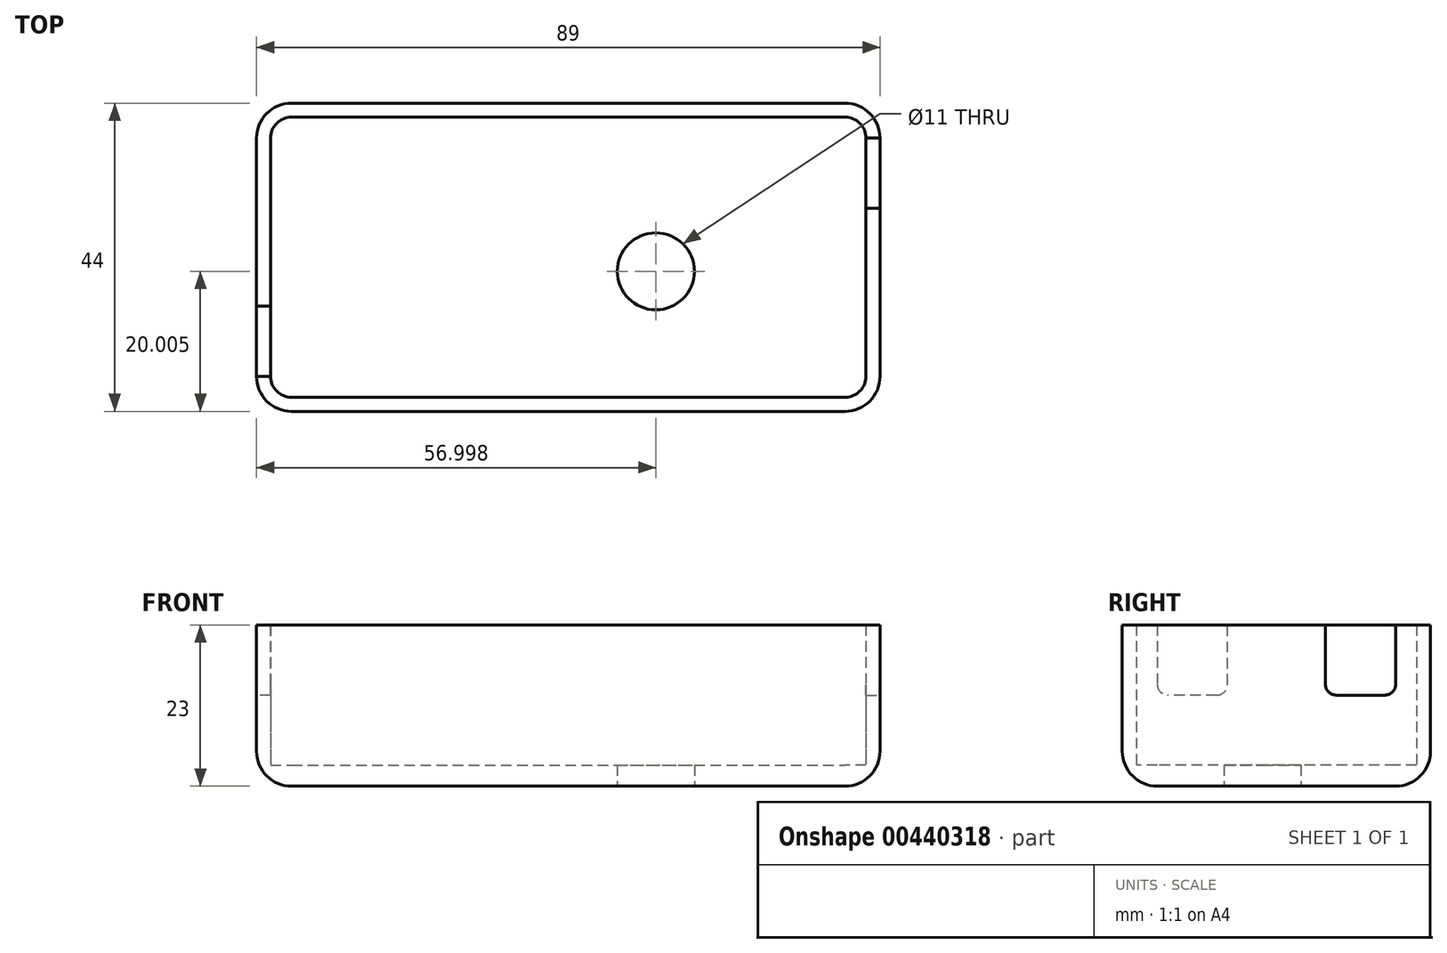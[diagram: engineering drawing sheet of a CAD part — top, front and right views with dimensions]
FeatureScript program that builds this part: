
annotation { "Feature Type Name" : "Feature", "Feature Type Description" : "" }
export const myFeature = defineFeature(function(context is Context, id is Id, definition is map)
    precondition{}
    {
        {
            var Q0;
            Q0=qCreatedBy(makeId("Top.planeOp"),FACE);
            var sketch = newSketch(context, id + "F0", { "sketchPlane" : qUnion([Q0])});
            skLineSegment(sketch, "E0.bottom", {"start": v(-41.95, 9.21) * mm, "end": v(43.05, 9.21) * mm});
            skLineSegment(sketch, "E0.top", {"start": v(-41.95, -30.79) * mm, "end": v(43.05, -30.79) * mm});
            skLineSegment(sketch, "E0.left", {"start": v(-41.95, 9.21) * mm, "end": v(-41.95, -30.79) * mm});
            skLineSegment(sketch, "E0.right", {"start": v(43.05, 9.21) * mm, "end": v(43.05, -30.79) * mm});
            skLineSegment(sketch, "E1.0", {"start": v(-43.95, -32.79) * mm, "end": v(45.05, -32.79) * mm});
            skLineSegment(sketch, "E1.1", {"start": v(-43.95, 11.21) * mm, "end": v(-43.95, -32.79) * mm});
            skLineSegment(sketch, "E1.2", {"start": v(-43.95, 11.21) * mm, "end": v(45.05, 11.21) * mm});
            skLineSegment(sketch, "E1.3", {"start": v(45.05, 11.21) * mm, "end": v(45.05, -32.79) * mm});
            skSolve(sketch);
        }
        {
            var Q0;
            Q0=makeQuery(id+"F0.imprint","IMPRINT",FACE,{"disambiguationData":[TD([[makeQuery(id+"F0.imprint","IMPRINT",EDGE,{"derivedFrom":sQuery(id+"F0.wireOp",EDGE,"E0.bottom")}),1.0]])]});
            extrude(context, id + "F1", {"entities" : qUnion([Q0]), "depth" : 20 * mm});
        }
        {
            var Q0;
            Q0=makeQuery(id+"F1.opExtrude","CAP_FACE",FACE,{"disambiguationData":[OSD([sQuery(id+"F0.wireOp",EDGE,"E0.bottom"),sQuery(id+"F0.wireOp",EDGE,"E0.top"),sQuery(id+"F0.wireOp",EDGE,"E0.left"),sQuery(id+"F0.wireOp",EDGE,"E0.right"),sQuery(id+"F0.wireOp",EDGE,"E1.0"),sQuery(id+"F0.wireOp",EDGE,"E1.1"),sQuery(id+"F0.wireOp",EDGE,"E1.2"),sQuery(id+"F0.wireOp",EDGE,"E1.3")])],"isStart":true});
            var sketch = newSketch(context, id + "F2", { "sketchPlane" : qUnion([Q0])});
            skLineSegment(sketch, "E2.bottom", {"start": v(-43.95, 32.79) * mm, "end": v(45.05, 32.79) * mm});
            skLineSegment(sketch, "E2.top", {"start": v(-43.95, -11.21) * mm, "end": v(45.05, -11.21) * mm});
            skLineSegment(sketch, "E2.left", {"start": v(-43.95, 32.79) * mm, "end": v(-43.95, -11.21) * mm});
            skLineSegment(sketch, "E2.right", {"start": v(45.05, 32.79) * mm, "end": v(45.05, -11.21) * mm});
            skSolve(sketch);
        }
        {
            var Q0;
            Q0=makeQuery(id+"F2.imprint","IMPRINT",FACE,{"disambiguationData":[TD([[makeQuery(id+"F2.imprint","IMPRINT",EDGE,{"derivedFrom":sQuery(id+"F2.wireOp",EDGE,"E2.bottom")}),-1.0]])]});
            var Q1;
            Q1=makeQuery(id+"F2.imprint","IMPRINT",FACE,{"disambiguationData":[TD([[makeQuery(id+"F2.imprint","IMPRINT",EDGE,{"derivedFrom":makeQuery(id+"F1.opExtrude","CAP_EDGE",EDGE,{"disambiguationData":[OSD([sQuery(id+"F0.wireOp",EDGE,"E0.bottom")])],"isStart":true})}),1.0]])]});
            extrude(context, id + "F3", {"entities" : qUnion([Q0, Q1]), "operationType" : NewBodyOperationType.ADD, "depth" : 3 * mm});
        }
        {
            var Q0;
            Q0=makeQuery(id+"F3.boolean.opBoolean","MERGE",EDGE,{"derivedFrom":[makeQuery(id+"F1.opExtrude","SWEPT_EDGE",EDGE,{"disambiguationData":[OSD([sQuery(id+"F0.wireOp",EDGE,"E1.0"),sQuery(id+"F0.wireOp",EDGE,"E1.1")])]}),makeQuery(id+"F3.opExtrude","SWEPT_EDGE",EDGE,{"disambiguationData":[OSD([sQuery(id+"F2.wireOp",EDGE,"E2.bottom"),sQuery(id+"F2.wireOp",EDGE,"E2.left")])]})]});
            var Q1;
            Q1=makeQuery(id+"F3.boolean.opBoolean","MERGE",EDGE,{"derivedFrom":[makeQuery(id+"F1.opExtrude","SWEPT_EDGE",EDGE,{"disambiguationData":[OSD([sQuery(id+"F0.wireOp",EDGE,"E1.0"),sQuery(id+"F0.wireOp",EDGE,"E1.3")])]}),makeQuery(id+"F3.opExtrude","SWEPT_EDGE",EDGE,{"disambiguationData":[OSD([sQuery(id+"F2.wireOp",EDGE,"E2.bottom"),sQuery(id+"F2.wireOp",EDGE,"E2.right")])]})]});
            var Q2;
            Q2=makeQuery(id+"F3.boolean.opBoolean","MERGE",EDGE,{"derivedFrom":[makeQuery(id+"F1.opExtrude","SWEPT_EDGE",EDGE,{"disambiguationData":[OSD([sQuery(id+"F0.wireOp",EDGE,"E1.2"),sQuery(id+"F0.wireOp",EDGE,"E1.3")])]}),makeQuery(id+"F3.opExtrude","SWEPT_EDGE",EDGE,{"disambiguationData":[OSD([sQuery(id+"F2.wireOp",EDGE,"E2.top"),sQuery(id+"F2.wireOp",EDGE,"E2.right")])]})]});
            var Q3;
            Q3=makeQuery(id+"F3.boolean.opBoolean","MERGE",EDGE,{"derivedFrom":[makeQuery(id+"F1.opExtrude","SWEPT_EDGE",EDGE,{"disambiguationData":[OSD([sQuery(id+"F0.wireOp",EDGE,"E1.1"),sQuery(id+"F0.wireOp",EDGE,"E1.2")])]}),makeQuery(id+"F3.opExtrude","SWEPT_EDGE",EDGE,{"disambiguationData":[OSD([sQuery(id+"F2.wireOp",EDGE,"E2.top"),sQuery(id+"F2.wireOp",EDGE,"E2.left")])]})]});
            var Q4;
            Q4=makeQuery(id+"F3.opExtrude","CAP_EDGE",EDGE,{"disambiguationData":[OSD([sQuery(id+"F2.wireOp",EDGE,"E2.left")])],"isStart":false});
            var Q5;
            Q5=makeQuery(id+"F3.opExtrude","CAP_EDGE",EDGE,{"disambiguationData":[OSD([sQuery(id+"F2.wireOp",EDGE,"E2.top")])],"isStart":false});
            var Q6;
            Q6=makeQuery(id+"F3.opExtrude","CAP_EDGE",EDGE,{"disambiguationData":[OSD([sQuery(id+"F2.wireOp",EDGE,"E2.right")])],"isStart":false});
            var Q7;
            Q7=makeQuery(id+"F3.opExtrude","CAP_EDGE",EDGE,{"disambiguationData":[OSD([sQuery(id+"F2.wireOp",EDGE,"E2.bottom")])],"isStart":false});
            fillet(context, id + "F4", {"entities" : qUnion([Q0, Q1, Q2, Q3, Q4, Q5, Q6, Q7]), "radius" : 5 * mm, "tangentPropagation" : true, "allowEdgeOverflow" : false});
        }
        {
            var Q0;
            Q0=makeQuery(id+"F1.opExtrude","SWEPT_EDGE",EDGE,{"disambiguationData":[OSD([sQuery(id+"F0.wireOp",EDGE,"E0.bottom"),sQuery(id+"F0.wireOp",EDGE,"E0.left")])]});
            var Q1;
            Q1=makeQuery(id+"F1.opExtrude","SWEPT_EDGE",EDGE,{"disambiguationData":[OSD([sQuery(id+"F0.wireOp",EDGE,"E0.top"),sQuery(id+"F0.wireOp",EDGE,"E0.left")])]});
            var Q2;
            Q2=makeQuery(id+"F1.opExtrude","SWEPT_EDGE",EDGE,{"disambiguationData":[OSD([sQuery(id+"F0.wireOp",EDGE,"E0.bottom"),sQuery(id+"F0.wireOp",EDGE,"E0.right")])]});
            var Q3;
            Q3=makeQuery(id+"F1.opExtrude","SWEPT_EDGE",EDGE,{"disambiguationData":[OSD([sQuery(id+"F0.wireOp",EDGE,"E0.top"),sQuery(id+"F0.wireOp",EDGE,"E0.right")])]});
            fillet(context, id + "F5", {"entities" : qUnion([Q0, Q1, Q2, Q3]), "radius" : 3 * mm, "tangentPropagation" : true, "allowEdgeOverflow" : false});
        }
        {
            var Q0;
            Q0=makeQuery(id+"F3.boolean.opBoolean","MERGE",FACE,{"derivedFrom":[makeQuery(id+"F1.opExtrude","SWEPT_FACE",FACE,{"disambiguationData":[OSD([sQuery(id+"F0.wireOp",EDGE,"E1.3")])]}),makeQuery(id+"F3.opExtrude","SWEPT_FACE",FACE,{"disambiguationData":[OSD([sQuery(id+"F2.wireOp",EDGE,"E2.right")])]})]});
            var sketch = newSketch(context, id + "F6", { "sketchPlane" : qUnion([Q0])});
            skLineSegment(sketch, "E3.bottom", {"start": v(6.21, 20) * mm, "end": v(-3.79, 20) * mm});
            skLineSegment(sketch, "E3.top", {"start": v(6.21, 10) * mm, "end": v(-3.79, 10) * mm});
            skLineSegment(sketch, "E3.left", {"start": v(6.21, 20) * mm, "end": v(6.21, 10) * mm});
            skLineSegment(sketch, "E3.right", {"start": v(-3.79, 20) * mm, "end": v(-3.79, 10) * mm});
            skSolve(sketch);
        }
        {
            var Q0;
            Q0=makeQuery(id+"F6.imprint","IMPRINT",FACE,{"disambiguationData":[TD([[makeQuery(id+"F6.imprint","IMPRINT",EDGE,{"derivedFrom":sQuery(id+"F6.wireOp",EDGE,"E3.bottom")}),1.0]])]});
            extrude(context, id + "F7", {"entities" : qUnion([Q0]), "operationType" : NewBodyOperationType.REMOVE, "oppositeDirection" : true, "depth" : 3 * mm});
        }
        {
            var Q0;
            Q0=makeQuery(id+"F3.boolean.opBoolean","MERGE",FACE,{"derivedFrom":[makeQuery(id+"F1.opExtrude","SWEPT_FACE",FACE,{"disambiguationData":[OSD([sQuery(id+"F0.wireOp",EDGE,"E1.1")])]}),makeQuery(id+"F3.opExtrude","SWEPT_FACE",FACE,{"disambiguationData":[OSD([sQuery(id+"F2.wireOp",EDGE,"E2.left")])]})]});
            var sketch = newSketch(context, id + "F8", { "sketchPlane" : qUnion([Q0])});
            skLineSegment(sketch, "E4.bottom", {"start": v(27.79, 20) * mm, "end": v(17.79, 20) * mm});
            skLineSegment(sketch, "E4.top", {"start": v(27.79, 10) * mm, "end": v(17.79, 10) * mm});
            skLineSegment(sketch, "E4.left", {"start": v(27.79, 20) * mm, "end": v(27.79, 10) * mm});
            skLineSegment(sketch, "E4.right", {"start": v(17.79, 20) * mm, "end": v(17.79, 10) * mm});
            skSolve(sketch);
        }
        {
            var Q0;
            Q0=makeQuery(id+"F8.imprint","IMPRINT",FACE,{"disambiguationData":[TD([[makeQuery(id+"F8.imprint","IMPRINT",EDGE,{"derivedFrom":sQuery(id+"F8.wireOp",EDGE,"E4.bottom")}),-1.0]])]});
            extrude(context, id + "F9", {"entities" : qUnion([Q0]), "operationType" : NewBodyOperationType.REMOVE, "oppositeDirection" : true, "depth" : 3 * mm});
        }
        {
            var Q0;
            Q0=makeQuery(id+"F7.boolean.opBoolean","COPY",EDGE,{"derivedFrom":makeQuery(id+"F7.opExtrude","SWEPT_EDGE",EDGE,{"disambiguationData":[OSD([sQuery(id+"F0.wireOp",EDGE,"E1.2"),sQuery(id+"F0.wireOp",EDGE,"E1.3"),sQuery(id+"F2.wireOp",EDGE,"E2.top"),sQuery(id+"F2.wireOp",EDGE,"E2.right"),sQuery(id+"F6.wireOp",EDGE,"E3.top"),sQuery(id+"F6.wireOp",EDGE,"E3.left")])]})});
            var Q1;
            Q1=makeQuery(id+"F7.boolean.opBoolean","COPY",EDGE,{"derivedFrom":makeQuery(id+"F7.opExtrude","SWEPT_EDGE",EDGE,{"disambiguationData":[OSD([sQuery(id+"F6.wireOp",EDGE,"E3.top"),sQuery(id+"F6.wireOp",EDGE,"E3.right")])]})});
            var Q2;
            Q2=makeQuery(id+"F9.boolean.opBoolean","COPY",EDGE,{"derivedFrom":makeQuery(id+"F9.opExtrude","SWEPT_EDGE",EDGE,{"disambiguationData":[OSD([sQuery(id+"F0.wireOp",EDGE,"E1.0"),sQuery(id+"F0.wireOp",EDGE,"E1.1"),sQuery(id+"F2.wireOp",EDGE,"E2.bottom"),sQuery(id+"F2.wireOp",EDGE,"E2.left"),sQuery(id+"F8.wireOp",EDGE,"E4.top"),sQuery(id+"F8.wireOp",EDGE,"E4.left")])]})});
            var Q3;
            Q3=makeQuery(id+"F9.boolean.opBoolean","COPY",EDGE,{"derivedFrom":makeQuery(id+"F9.opExtrude","SWEPT_EDGE",EDGE,{"disambiguationData":[OSD([sQuery(id+"F8.wireOp",EDGE,"E4.top"),sQuery(id+"F8.wireOp",EDGE,"E4.right")])]})});
            fillet(context, id + "F10", {"entities" : qUnion([Q0, Q1, Q2, Q3]), "radius" : 1.5 * mm, "tangentPropagation" : true, "allowEdgeOverflow" : false});
        }
        {
            var Q0;
            Q0=makeQuery(id+"F3.opExtrude","CAP_FACE",FACE,{"disambiguationData":[OSD([sQuery(id+"F2.wireOp",EDGE,"E2.bottom"),sQuery(id+"F2.wireOp",EDGE,"E2.top"),sQuery(id+"F2.wireOp",EDGE,"E2.left"),sQuery(id+"F2.wireOp",EDGE,"E2.right")])],"isStart":false});
            var sketch = newSketch(context, id + "F11", { "sketchPlane" : qUnion([Q0])});
            skLineSegment(sketch, "E5", {"start": v(-38.95, 27.79) * mm, "end": v(13.05, 27.79) * mm});
            skLineSegment(sketch, "E6", {"start": v(13.05, 27.79) * mm, "end": v(13.05, 12.79) * mm});
            skCircle(sketch, "E7", {"center": v(13.05, 12.79) * mm, "radius": 5.5 * mm});
            skSolve(sketch);
        }
        {
            var Q0;
            Q0=makeQuery(id+"F11.imprint","IMPRINT",FACE,{"disambiguationData":[TD([[makeQuery(id+"F11.imprint","IMPRINT",EDGE,{"derivedFrom":sQuery(id+"F11.wireOp",EDGE,"E7")}),1.0]])]});
            extrude(context, id + "F12", {"entities" : qUnion([Q0]), "operationType" : NewBodyOperationType.REMOVE, "oppositeDirection" : true, "depth" : 25 * mm});
        }
        {
            var Q0;
            Q0=makeQuery(id+"F1.opExtrude","SWEPT_BODY",BODY,{"disambiguationData":[OSD([sQuery(id+"F0.wireOp",EDGE,"E0.bottom"),sQuery(id+"F0.wireOp",EDGE,"E0.top"),sQuery(id+"F0.wireOp",EDGE,"E0.left"),sQuery(id+"F0.wireOp",EDGE,"E0.right"),sQuery(id+"F0.wireOp",EDGE,"E1.0"),sQuery(id+"F0.wireOp",EDGE,"E1.1"),sQuery(id+"F0.wireOp",EDGE,"E1.2"),sQuery(id+"F0.wireOp",EDGE,"E1.3")])]});
            transform(context, id + "F13", {"entities" : qUnion([Q0]), "transformType" : TransformType.TRANSLATION_3D, "dx" : 0 * mm, "dy" : 0 * mm, "dz" : 30 * mm, "makeCopy" : true});
        }
        {
            var Q0;
            Q0=makeQuery(id+"F13.opPattern","COPY",BODY,{"derivedFrom":makeQuery(id+"F1.opExtrude","SWEPT_BODY",BODY,{"disambiguationData":[OSD([sQuery(id+"F0.wireOp",EDGE,"E0.bottom"),sQuery(id+"F0.wireOp",EDGE,"E0.top"),sQuery(id+"F0.wireOp",EDGE,"E0.left"),sQuery(id+"F0.wireOp",EDGE,"E0.right"),sQuery(id+"F0.wireOp",EDGE,"E1.0"),sQuery(id+"F0.wireOp",EDGE,"E1.1"),sQuery(id+"F0.wireOp",EDGE,"E1.2"),sQuery(id+"F0.wireOp",EDGE,"E1.3")])]}),"instanceName":"1"});
            deleteBodies(context, id + "F14", {"entities" : qUnion([Q0])});
        }
    });
